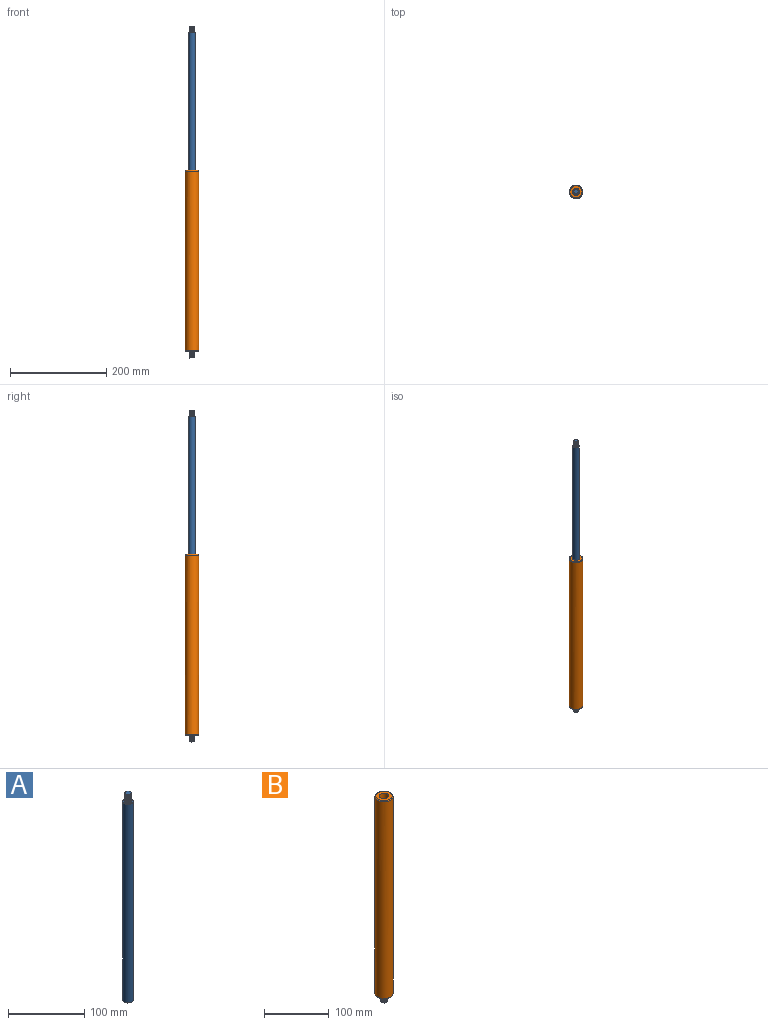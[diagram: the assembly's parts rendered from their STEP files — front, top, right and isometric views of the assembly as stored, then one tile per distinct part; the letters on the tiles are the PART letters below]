
ASSEMBLY  parts=2 mates=1
PART A: 46 faces, bbox 14.1x14.1x333.8 mm
  f0: cylinder r=6.99mm len=319.47mm, axis (0,0,-1), area 14020.8mm2, adj f1,f2
  f1: plane 14.08x14.08mm, normal (0,0,1), area 81.4mm2, adj f0,f3,f4,f5,f6,f7
  f2: plane 13.97x13.97mm, normal (0,0,-1), area 153.3mm2, adj f0
  f3: cone r=5.18mm half-angle=60deg, axis (0,0.15,-0.99), area 7.8mm2, adj f1,f4,f7
  f4: cylinder r=4.37mm len=8.74mm, axis (0,0.15,-0.99), area 5.7mm2, adj f1,f3,f6
  f5: cylinder r=5mm len=10mm, axis (0,0,1), area 10.2mm2, adj f1,f6,f8
  f6: cone r=4.37mm half-angle=60deg, axis (0,-0.15,0.99), area 15.8mm2, adj f1,f4,f5
  f7: cylinder r=5mm len=8.12mm, axis (0,0,1), area 1.5mm2, adj f1,f3
  f8: cone r=5.18mm half-angle=60deg, axis (0,0.15,-0.99), area 22.6mm2, adj f5,f9
  f9: cylinder r=4.37mm len=8.74mm, axis (0,0.15,-0.99), area 10.3mm2, adj f8,f10
  f10: cone r=4.37mm half-angle=60deg, axis (0,-0.15,0.99), area 22.6mm2, adj f9,f11
  f11: cylinder r=5mm len=10mm, axis (0,0,1), area 10.9mm2, adj f10,f12
  f12: cone r=5.18mm half-angle=60deg, axis (0,0.15,-0.99), area 22.6mm2, adj f11,f13
  f13: cylinder r=4.37mm len=8.74mm, axis (0,0.15,-0.99), area 10.3mm2, adj f12,f14
  f14: cone r=4.37mm half-angle=60deg, axis (0,-0.15,0.99), area 22.6mm2, adj f13,f15
  f15: cylinder r=5mm len=10mm, axis (0,0,1), area 10.9mm2, adj f14,f16
  f16: cone r=5.18mm half-angle=60deg, axis (0,0.15,-0.99), area 22.6mm2, adj f15,f17
  f17: cylinder r=4.37mm len=8.74mm, axis (0,0.15,-0.99), area 10.3mm2, adj f16,f18
  f18: cone r=4.37mm half-angle=60deg, axis (0,-0.15,0.99), area 22.6mm2, adj f17,f19
  f19: cylinder r=5mm len=10mm, axis (0,0,1), area 10.9mm2, adj f18,f20
  f20: cone r=5.18mm half-angle=60deg, axis (0,0.15,-0.99), area 22.6mm2, adj f19,f21
  f21: cylinder r=4.37mm len=8.74mm, axis (0,0.15,-0.99), area 10.3mm2, adj f20,f22
  f22: cone r=4.37mm half-angle=60deg, axis (0,-0.15,0.99), area 22.6mm2, adj f21,f23
  f23: cylinder r=5mm len=10mm, axis (0,0,1), area 10.9mm2, adj f22,f24
  f24: cone r=5.18mm half-angle=60deg, axis (0,0.15,-0.99), area 22.6mm2, adj f23,f25
  f25: cylinder r=4.37mm len=8.74mm, axis (0,0.15,-0.99), area 10.3mm2, adj f24,f26
  f26: cone r=4.37mm half-angle=60deg, axis (0,-0.15,0.99), area 22.6mm2, adj f25,f27
  f27: cylinder r=5mm len=10mm, axis (0,0,1), area 10.9mm2, adj f26,f28
  f28: cone r=5.18mm half-angle=60deg, axis (0,0.15,-0.99), area 22.6mm2, adj f27,f29
  f29: cylinder r=4.37mm len=8.74mm, axis (0,0.15,-0.99), area 10.3mm2, adj f28,f30
  f30: cone r=4.37mm half-angle=60deg, axis (0,-0.15,0.99), area 22.6mm2, adj f29,f31
  f31: cylinder r=5mm len=10mm, axis (0,0,1), area 10.9mm2, adj f30,f32
  f32: cone r=5.18mm half-angle=60deg, axis (0,0.15,-0.99), area 22.6mm2, adj f31,f33
  f33: cylinder r=4.37mm len=8.74mm, axis (0,0.15,-0.99), area 10.3mm2, adj f32,f34
  f34: cone r=4.37mm half-angle=60deg, axis (0,-0.15,0.99), area 22.6mm2, adj f33,f35
  f35: cylinder r=5mm len=10mm, axis (0,0,1), area 10.9mm2, adj f34,f36
  f36: cone r=5.18mm half-angle=60deg, axis (0,0.15,-0.99), area 22.6mm2, adj f35,f37
  f37: cylinder r=4.37mm len=8.74mm, axis (0,0.15,-0.99), area 10.3mm2, adj f36,f38
  f38: cone r=4.37mm half-angle=60deg, axis (0,-0.15,0.99), area 18.1mm2, adj f37,f39,f40,f41
  f39: cone r=5mm half-angle=25deg, axis (0,0,-1), area 23.1mm2, adj f38,f40,f41,f42,f43,f44,f45
  f40: cone r=5mm half-angle=25deg, axis (0,0,-1), area 1.6mm2, adj f38,f39,f41,f44
  f41: cylinder r=5mm len=9.66mm, axis (0,0,1), area 3.7mm2, adj f38,f39,f40,f44
  f42: cone r=4.37mm half-angle=60deg, axis (0,-0.15,0.99), area 2.6mm2, adj f39,f45
  f43: plane 8.59x8.59mm, normal (0,0,1), area 57.9mm2, adj f39
  f44: cone r=5.18mm half-angle=60deg, axis (0,0.15,-0.99), area 11mm2, adj f39,f40,f41,f45
  f45: cylinder r=4.37mm len=8.74mm, axis (0,0.15,-0.99), area 6.3mm2, adj f39,f42,f44
PART B: 50 faces, bbox 30.4x30.4x389.5 mm
  f0: cone r=4.37mm half-angle=60deg, axis (0,0.15,-0.99), area 2.6mm2, adj f1,f3
  f1: cone r=5mm half-angle=25deg, axis (0,0,1), area 23.1mm2, adj f0,f2,f3,f4,f5,f6,f7
  f2: cone r=5mm half-angle=25deg, axis (0,0,1), area 1.6mm2, adj f1,f5,f6,f7
  f3: cylinder r=4.37mm len=8.74mm, axis (0,-0.15,0.99), area 6.3mm2, adj f0,f1,f5
  f4: plane 8.59x8.59mm, normal (0,0,-1), area 57.9mm2, adj f1
  f5: cone r=5.18mm half-angle=60deg, axis (0,-0.15,0.99), area 11.3mm2, adj f1,f2,f3,f7
  f6: cone r=4.37mm half-angle=60deg, axis (0,0.15,-0.99), area 18.2mm2, adj f1,f2,f7,f8
  f7: cylinder r=5mm len=9.66mm, axis (0,0,-1), area 2.7mm2, adj f1,f2,f5,f6
  f8: cylinder r=4.37mm len=8.74mm, axis (0,-0.15,0.99), area 10.3mm2, adj f6,f9
  f9: cone r=5.18mm half-angle=60deg, axis (0,-0.15,0.99), area 23.7mm2, adj f8,f10
  f10: cylinder r=5mm len=10mm, axis (0,0,-1), area 10.9mm2, adj f9,f11
  f11: cone r=4.37mm half-angle=60deg, axis (0,0.15,-0.99), area 23.7mm2, adj f10,f12
  f12: cylinder r=4.37mm len=8.74mm, axis (0,-0.15,0.99), area 10.3mm2, adj f11,f13
  f13: cone r=5.18mm half-angle=60deg, axis (0,-0.15,0.99), area 23.7mm2, adj f12,f14
  f14: cylinder r=5mm len=10mm, axis (0,0,-1), area 10.9mm2, adj f13,f15
  f15: cone r=4.37mm half-angle=60deg, axis (0,0.15,-0.99), area 23.7mm2, adj f14,f16
  f16: cylinder r=4.37mm len=8.74mm, axis (0,-0.15,0.99), area 10.3mm2, adj f15,f17
  f17: cone r=5.18mm half-angle=60deg, axis (0,-0.15,0.99), area 23.7mm2, adj f16,f18
  f18: cylinder r=5mm len=10mm, axis (0,0,-1), area 10.9mm2, adj f17,f19
  f19: cone r=4.37mm half-angle=60deg, axis (0,0.15,-0.99), area 23.7mm2, adj f18,f20
  f20: cylinder r=4.37mm len=8.74mm, axis (0,-0.15,0.99), area 10.3mm2, adj f19,f21
  f21: cone r=5.18mm half-angle=60deg, axis (0,-0.15,0.99), area 23.7mm2, adj f20,f22
  f22: cylinder r=5mm len=10mm, axis (0,0,-1), area 10.9mm2, adj f21,f23
  f23: cone r=4.37mm half-angle=60deg, axis (0,0.15,-0.99), area 23.7mm2, adj f22,f24
  f24: cylinder r=4.37mm len=8.74mm, axis (0,-0.15,0.99), area 10.3mm2, adj f23,f25
  f25: cone r=5.18mm half-angle=60deg, axis (0,-0.15,0.99), area 23.7mm2, adj f24,f26
  f26: cylinder r=5mm len=10mm, axis (0,0,-1), area 10.9mm2, adj f25,f27
  f27: cone r=4.37mm half-angle=60deg, axis (0,0.15,-0.99), area 23.7mm2, adj f26,f28
  f28: cylinder r=4.37mm len=8.74mm, axis (0,-0.15,0.99), area 10.3mm2, adj f27,f29
  f29: cone r=5.18mm half-angle=60deg, axis (0,-0.15,0.99), area 23.7mm2, adj f28,f30
  f30: cylinder r=5mm len=10mm, axis (0,0,-1), area 10.9mm2, adj f29,f31
  f31: cone r=4.37mm half-angle=60deg, axis (0,0.15,-0.99), area 23.7mm2, adj f30,f32
  f32: cylinder r=4.37mm len=8.74mm, axis (0,-0.15,0.99), area 10.3mm2, adj f31,f33
  f33: cone r=5.18mm half-angle=60deg, axis (0,-0.15,0.99), area 23.7mm2, adj f32,f34
  f34: cylinder r=5mm len=10mm, axis (0,0,-1), area 10.9mm2, adj f33,f35
  f35: cone r=4.37mm half-angle=60deg, axis (0,0.15,-0.99), area 23.7mm2, adj f34,f36
  f36: cylinder r=4.37mm len=8.74mm, axis (0,-0.15,0.99), area 10.3mm2, adj f35,f37
  f37: cone r=5.18mm half-angle=60deg, axis (0,-0.15,0.99), area 23.7mm2, adj f36,f38
  f38: cylinder r=5mm len=10mm, axis (0,0,-1), area 10.6mm2, adj f37,f39,f40
  f39: cone r=4.37mm half-angle=60deg, axis (0,0.15,-0.99), area 17.8mm2, adj f38,f40,f41
  f40: plane 25.32x25.32mm, normal (0,0,-1), area 427.1mm2, adj f38,f39,f41,f42,f43,f44
  f41: cylinder r=4.37mm len=8.74mm, axis (0,-0.15,0.99), area 5.7mm2, adj f39,f40,f43
  f42: torus R=12.6mm, axis (0,0,1), area 181.8mm2, adj f40,f45
  f43: cone r=5.18mm half-angle=60deg, axis (0,-0.15,0.99), area 7.8mm2, adj f40,f41,f44
  f44: cylinder r=5mm len=8.12mm, axis (0,0,-1), area 1.5mm2, adj f40,f43
  f45: cylinder r=13.97mm len=372.42mm, axis (0,0,1), area 32689.9mm2, adj f42,f46
  f46: torus R=12.6mm, axis (0,0,-1), area 181.8mm2, adj f45,f47
  f47: plane 25.21x25.21mm, normal (0,0,1), area 339.1mm2, adj f46,f48
  f48: cylinder r=7.13mm len=319.47mm, axis (0,0,1), area 14321.9mm2, adj f47,f49
  f49: plane 14.27x14.27mm, normal (0,0,1), area 159.9mm2, adj f48
PLACE A rot(axis=(-0.23,-0.96,-0.17),0deg) t=(-17.52,93.56,-43.17)mm
PLACE B rot(axis=(-0.23,-0.96,-0.17),0deg) t=(-17.52,93.56,-23.74)mm
MATE slider B.f1 <-> A.f0  axis (0,0,1) through (-17.52,93.56,10.07)mm
